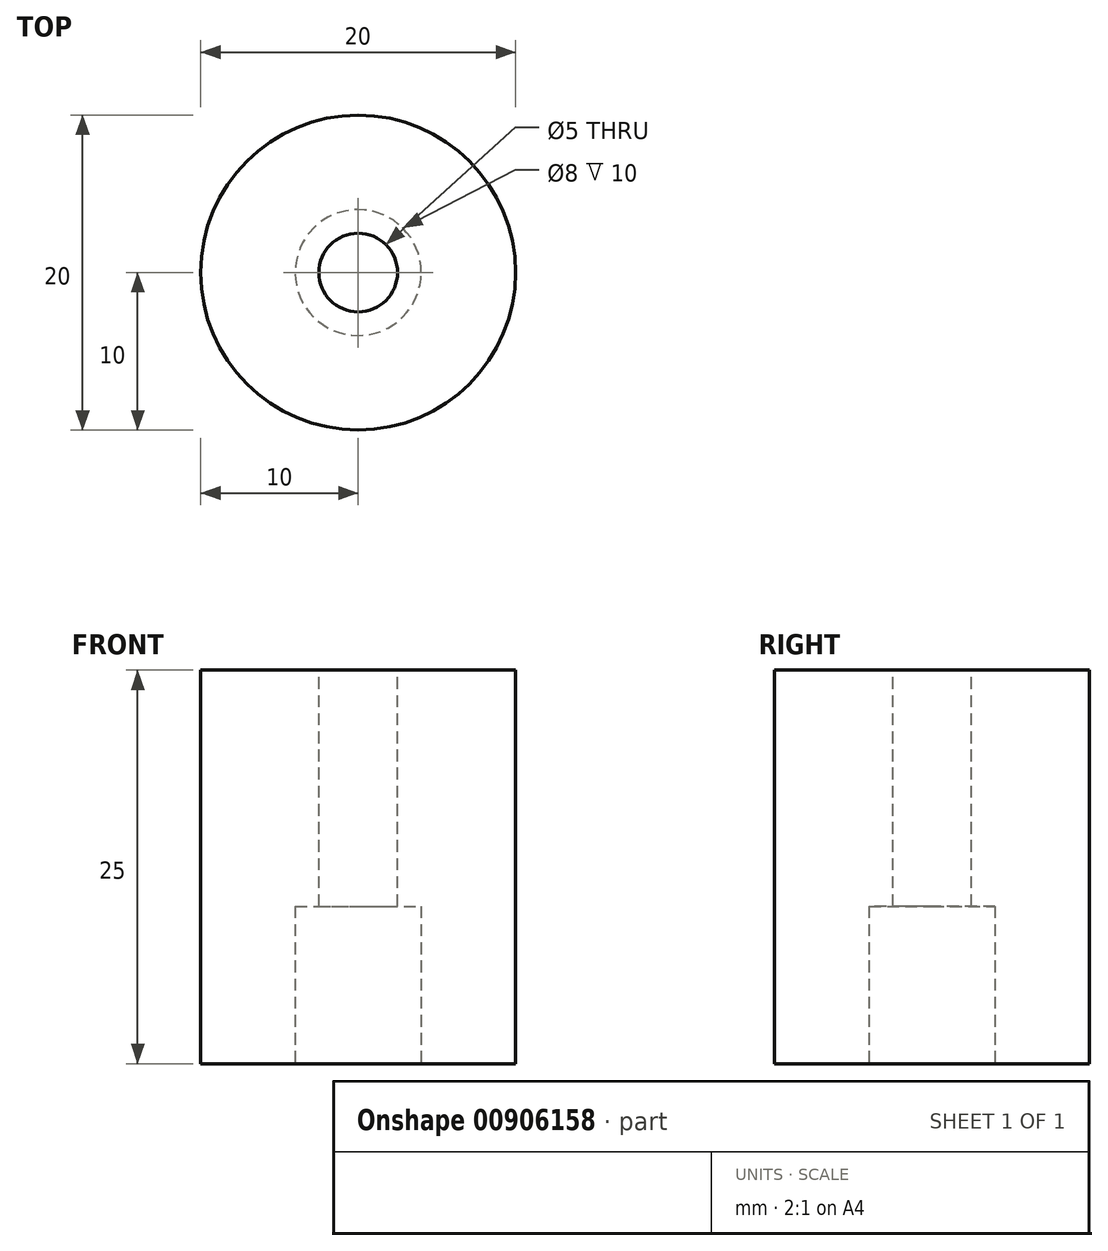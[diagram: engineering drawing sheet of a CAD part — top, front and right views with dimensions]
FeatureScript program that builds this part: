
annotation { "Feature Type Name" : "Feature", "Feature Type Description" : "" }
export const myFeature = defineFeature(function(context is Context, id is Id, definition is map)
    precondition{}
    {
        {
            var Q0;
            Q0=qCreatedBy(makeId("Top.planeOp"),FACE);
            var sketch = newSketch(context, id + "F0", { "sketchPlane" : qUnion([Q0])});
            skCircle(sketch, "E0", {"center": v(0, 0) * mm, "radius": 10 * mm});
            skSolve(sketch);
        }
        {
            var Q0;
            Q0 = qSketchRegion(id + "F0", true);
            extrude(context, id + "F1", {"entities" : qUnion([Q0]), "depth" : 7.5 * mm, "offsetDistance" : 25 * mm});
        }
        {
            var Q0;
            Q0=makeQuery(id+"F1.opExtrude","CAP_FACE",FACE,{"disambiguationData":[OSD([sQuery(id+"F0.wireOp",EDGE,"E0")])],"isStart":false});
            var sketch = newSketch(context, id + "F2", { "sketchPlane" : qUnion([Q0])});
            skCircle(sketch, "E1", {"center": v(0, 0) * mm, "radius": 10 * mm});
            skSolve(sketch);
        }
        {
            var Q0;
            Q0 = qSketchRegion(id + "F2", true);
            extrude(context, id + "F3", {"entities" : qUnion([Q0]), "operationType" : NewBodyOperationType.ADD, "depth" : 10 * mm, "offsetDistance" : 25 * mm});
        }
        {
            var Q0;
            Q0=makeQuery(id+"F3.opExtrude","CAP_FACE",FACE,{"disambiguationData":[OSD([sQuery(id+"F2.wireOp",EDGE,"E1")])],"isStart":false});
            var sketch = newSketch(context, id + "F4", { "sketchPlane" : qUnion([Q0])});
            skCircle(sketch, "E2", {"center": v(0, 0) * mm, "radius": 10 * mm});
            skSolve(sketch);
        }
        {
            var Q0;
            Q0 = qSketchRegion(id + "F4", true);
            extrude(context, id + "F5", {"entities" : qUnion([Q0]), "operationType" : NewBodyOperationType.ADD, "depth" : 7.5 * mm, "offsetDistance" : 25 * mm});
        }
        {
            var Q0;
            Q0=makeQuery(id+"F5.opExtrude","CAP_FACE",FACE,{"disambiguationData":[OSD([sQuery(id+"F4.wireOp",EDGE,"E2")])],"isStart":false});
            var sketch = newSketch(context, id + "F6", { "sketchPlane" : qUnion([Q0])});
            skCircle(sketch, "E3", {"center": v(0, 0) * mm, "radius": 2.5 * mm});
            skSolve(sketch);
        }
        {
            var Q0;
            Q0 = qSketchRegion(id + "F6", true);
            extrude(context, id + "F7", {"entities" : qUnion([Q0]), "operationType" : NewBodyOperationType.REMOVE, "oppositeDirection" : true, "depth" : 25 * mm, "offsetDistance" : 25 * mm});
        }
        {
            var Q0;
            Q0=makeQuery(id+"F1.opExtrude","CAP_FACE",FACE,{"disambiguationData":[OSD([sQuery(id+"F0.wireOp",EDGE,"E0")])],"isStart":true});
            var sketch = newSketch(context, id + "F8", { "sketchPlane" : qUnion([Q0])});
            skCircle(sketch, "E4", {"center": v(0, 0) * mm, "radius": 4 * mm});
            skSolve(sketch);
        }
        {
            var Q0;
            Q0 = qSketchRegion(id + "F8", true);
            extrude(context, id + "F9", {"entities" : qUnion([Q0]), "operationType" : NewBodyOperationType.REMOVE, "oppositeDirection" : true, "depth" : 10 * mm, "offsetDistance" : 25 * mm});
        }
    });
